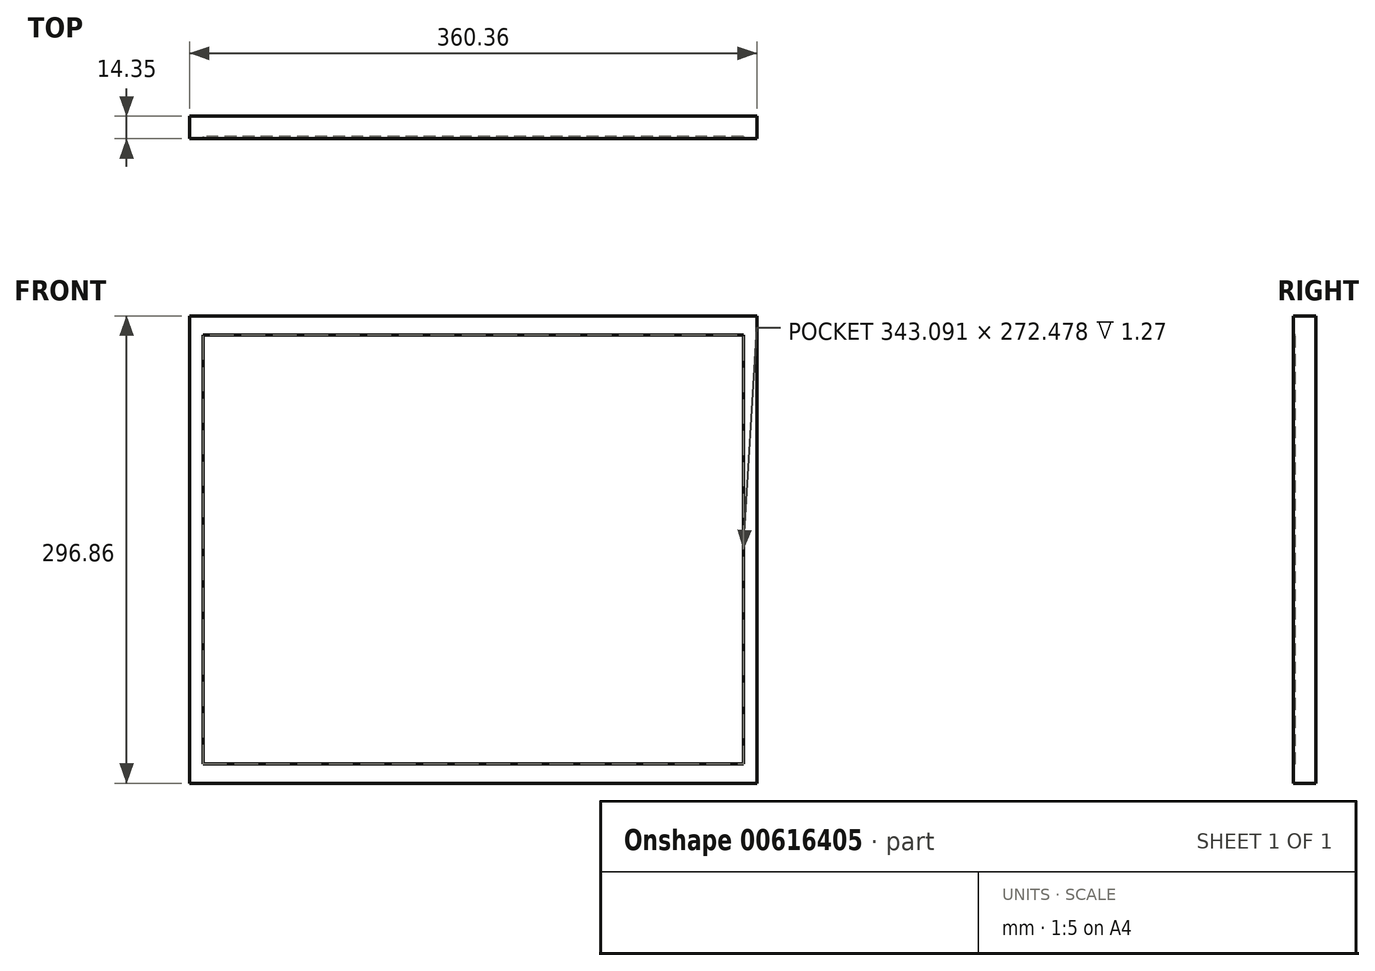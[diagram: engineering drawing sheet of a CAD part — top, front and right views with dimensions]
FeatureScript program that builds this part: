
annotation { "Feature Type Name" : "Feature", "Feature Type Description" : "" }
export const myFeature = defineFeature(function(context is Context, id is Id, definition is map)
    precondition{}
    {
        {
            var Q0;
            Q0=qCreatedBy(makeId("Front.planeOp"),FACE);
            var sketch = newSketch(context, id + "F0", { "sketchPlane" : qUnion([Q0])});
            skLineSegment(sketch, "E0.bottom", {"start": v(180.18, -148.43) * mm, "end": v(-180.18, -148.43) * mm});
            skLineSegment(sketch, "E0.top", {"start": v(180.18, 148.43) * mm, "end": v(-180.18, 148.43) * mm});
            skLineSegment(sketch, "E0.left", {"start": v(180.18, -148.43) * mm, "end": v(180.18, 148.43) * mm});
            skLineSegment(sketch, "E0.right", {"start": v(-180.18, -148.43) * mm, "end": v(-180.18, 148.43) * mm});
            skPoint(sketch, "E0.middle", {"position": v(0, 0) * mm});
            skSolve(sketch);
        }
        {
            var Q0;
            Q0=qSketchRegion(id+"F0",true);
            extrude(context, id + "F1", {"entities" : qUnion([Q0]), "depth" : 14.35 * mm});
        }
        {
            var Q0;
            Q0=makeQuery(id+"F1.opExtrude","CAP_FACE",FACE,{"disambiguationData":[OSD([sQuery(id+"F0.wireOp",EDGE,"E0.bottom"),sQuery(id+"F0.wireOp",EDGE,"E0.top"),sQuery(id+"F0.wireOp",EDGE,"E0.left"),sQuery(id+"F0.wireOp",EDGE,"E0.right")])],"isStart":false});
            var sketch = newSketch(context, id + "F2", { "sketchPlane" : qUnion([Q0])});
            skLineSegment(sketch, "E1.bottom", {"start": v(171.55, -136.24) * mm, "end": v(-171.55, -136.24) * mm});
            skLineSegment(sketch, "E1.top", {"start": v(171.55, 136.24) * mm, "end": v(-171.55, 136.24) * mm});
            skLineSegment(sketch, "E1.left", {"start": v(171.55, -136.24) * mm, "end": v(171.55, 136.24) * mm});
            skLineSegment(sketch, "E1.right", {"start": v(-171.55, -136.24) * mm, "end": v(-171.55, 136.24) * mm});
            skPoint(sketch, "E1.middle", {"position": v(0, 0) * mm});
            skSolve(sketch);
        }
        {
            var Q0;
            Q0=makeQuery(id+"F2.imprint","IMPRINT",FACE,{"disambiguationData":[TD([[makeQuery(id+"F2.imprint","IMPRINT",EDGE,{"derivedFrom":sQuery(id+"F2.wireOp",EDGE,"E1.bottom")}),-1.0]])]});
            extrude(context, id + "F3", {"entities" : qUnion([Q0]), "operationType" : NewBodyOperationType.REMOVE, "oppositeDirection" : true, "depth" : 1.27 * mm});
        }
    });
